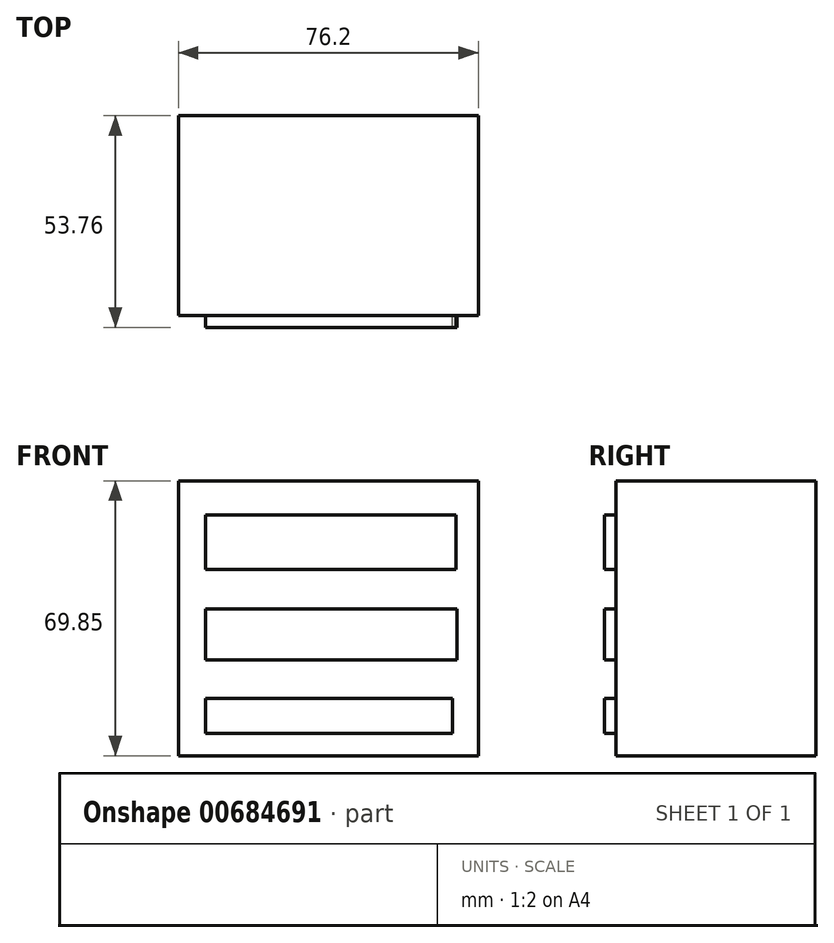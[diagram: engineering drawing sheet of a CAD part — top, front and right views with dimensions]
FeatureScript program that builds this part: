
annotation { "Feature Type Name" : "Feature", "Feature Type Description" : "" }
export const myFeature = defineFeature(function(context is Context, id is Id, definition is map)
    precondition{}
    {
        {
            var Q0;
            Q0=qCreatedBy(makeId("Top.planeOp"),FACE);
            var sketch = newSketch(context, id + "F0", { "sketchPlane" : qUnion([Q0])});
            skLineSegment(sketch, "E0.bottom", {"start": v(-35.26, 28.36) * mm, "end": v(40.94, 28.36) * mm});
            skLineSegment(sketch, "E0.top", {"start": v(-35.26, -22.44) * mm, "end": v(40.94, -22.44) * mm});
            skLineSegment(sketch, "E0.left", {"start": v(-35.26, 28.36) * mm, "end": v(-35.26, -22.44) * mm});
            skLineSegment(sketch, "E0.right", {"start": v(40.94, 28.36) * mm, "end": v(40.94, -22.44) * mm});
            skSolve(sketch);
        }
        {
            var Q0;
            Q0=qSketchRegion(id+"F0",true);
            extrude(context, id + "F1", {"entities" : qUnion([Q0]), "depth" : 69.85 * mm, "offsetDistance" : 25.4 * mm});
        }
        {
            var Q0;
            Q0=qCreatedBy(makeId("Front.planeOp"),FACE);
            var sketch = newSketch(context, id + "F2", { "sketchPlane" : qUnion([Q0])});
            skLineSegment(sketch, "E1.bottom", {"start": v(-28.35, 61.17) * mm, "end": v(35.26, 61.17) * mm});
            skLineSegment(sketch, "E1.top", {"start": v(-28.35, 47.35) * mm, "end": v(35.26, 47.35) * mm});
            skLineSegment(sketch, "E1.left", {"start": v(-28.35, 61.17) * mm, "end": v(-28.35, 47.35) * mm});
            skLineSegment(sketch, "E1.right", {"start": v(35.26, 61.17) * mm, "end": v(35.26, 47.35) * mm});
            skLineSegment(sketch, "E2.bottom", {"start": v(-28.35, 37.28) * mm, "end": v(35.55, 37.28) * mm});
            skLineSegment(sketch, "E2.top", {"start": v(-28.35, 24.33) * mm, "end": v(35.55, 24.33) * mm});
            skLineSegment(sketch, "E2.left", {"start": v(-28.35, 37.28) * mm, "end": v(-28.35, 24.33) * mm});
            skLineSegment(sketch, "E2.right", {"start": v(35.55, 37.28) * mm, "end": v(35.55, 24.33) * mm});
            skLineSegment(sketch, "E3.bottom", {"start": v(-28.35, 14.54) * mm, "end": v(34.4, 14.54) * mm});
            skLineSegment(sketch, "E3.top", {"start": v(-28.35, 5.62) * mm, "end": v(34.4, 5.62) * mm});
            skLineSegment(sketch, "E3.left", {"start": v(-28.35, 14.54) * mm, "end": v(-28.35, 5.62) * mm});
            skLineSegment(sketch, "E3.right", {"start": v(34.4, 14.54) * mm, "end": v(34.4, 5.62) * mm});
            skSolve(sketch);
        }
        {
            var Q0;
            Q0=qSketchRegion(id+"F2",true);
            extrude(context, id + "F3", {"entities" : qUnion([Q0]), "operationType" : NewBodyOperationType.ADD, "depth" : 25.4 * mm, "offsetDistance" : 25.4 * mm});
        }
    });
